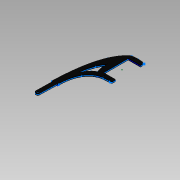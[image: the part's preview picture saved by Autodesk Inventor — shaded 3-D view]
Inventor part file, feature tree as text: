
AUTODESK INVENTOR PART (.ipt)
format: ipt  version: 2015 SP1 (Build 190203100, 203)  size: 164,352 bytes
history: native  units: mm
features: fillet x3, extrude x2, sketch x1
ambient origin geometry x8: Origin, YZ Plane, XZ Plane, XY Plane, X Axis, Y Axis, Z Axis, Center Point
bodies: Solid1 (feature_tree)
feature tree (6):
  sketch  "Sketch1"  dims[d2=6.0mm d3=20.45mm d4=21.0mm d5=2.2352mm d6=5.16mm d7=3.64mm d8=42.0mm d9=3.3mm d11=42.0mm d12=8.67mm d17=1.3mm d18=1.3mm d19=6.7mm d20=2.0mm d21=2.2352mm d22=9.8044mm d23=2.2352mm d24=2.2352mm d25=9.8044mm d26=49.1998mm d27=3.5mm d28=0.0mm d29=9.0mm d30=4.0mm d31=0.25mm d34=131.9mm d35=3.285mm d36=10.0mm d37=0.0mm]
  extrude  "Extrusion1"  Depth=10.0mm
  fillet  "Fillet1"  Radius=21.0mm
  fillet  "Fillet2"  Radius=2.2352mm
  fillet  "Fillet3"  Radius=5.16mm
  extrude  "Extrusion2"  Depth=10.0mm
